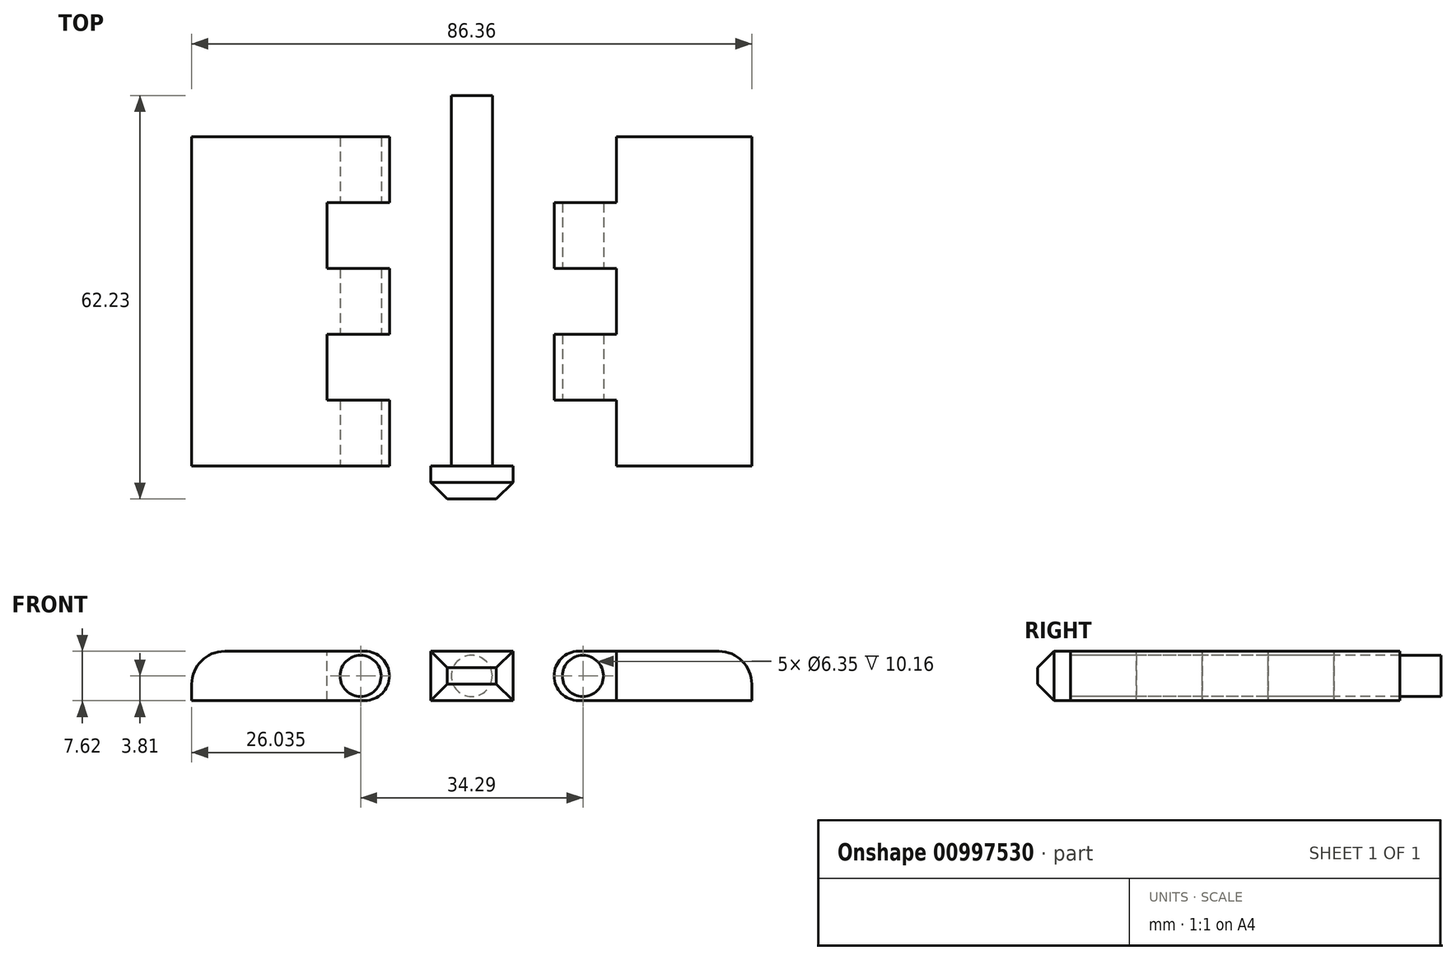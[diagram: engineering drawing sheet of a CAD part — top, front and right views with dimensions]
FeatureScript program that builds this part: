
annotation { "Feature Type Name" : "Feature", "Feature Type Description" : "" }
export const myFeature = defineFeature(function(context is Context, id is Id, definition is map)
    precondition{}
    {
        {
            var Q0;
            Q0=qCreatedBy(makeId("Top.planeOp"),FACE);
            var sketch = newSketch(context, id + "F0", { "sketchPlane" : qUnion([Q0])});
            skLineSegment(sketch, "E0.bottom", {"start": v(0, 0) * mm, "end": v(30.48, 0) * mm});
            skLineSegment(sketch, "E0.top", {"start": v(0, 50.8) * mm, "end": v(30.48, 50.8) * mm});
            skLineSegment(sketch, "E0.left", {"start": v(0, 0) * mm, "end": v(0, 50.8) * mm});
            skLineSegment(sketch, "E0.right", {"start": v(30.48, 0) * mm, "end": v(30.48, 50.8) * mm});
            skPoint(sketch, "E1.startSnap0", {"position": v(30.48, 25.4) * mm});
            skLineSegment(sketch, "E2", {"start": v(-12.7, 75.24) * mm, "end": v(-12.7, -23.42) * mm, "construction": true});
            skLineSegment(sketch, "E3.MirrorCS", {"start": v(-55.88, 0) * mm, "end": v(-55.88, 50.8) * mm});
            skLineSegment(sketch, "E4.MirrorCS", {"start": v(-25.4, 50.8) * mm, "end": v(-55.88, 50.8) * mm});
            skPoint(sketch, "E5.MirrorP", {"position": v(-55.88, 25.4) * mm});
            skLineSegment(sketch, "E6.MirrorCS", {"start": v(-25.4, 0) * mm, "end": v(-55.88, 0) * mm});
            skLineSegment(sketch, "E7.MirrorCS", {"start": v(-25.4, 0) * mm, "end": v(-25.4, 50.8) * mm});
            skSolve(sketch);
        }
        {
            var Q0;
            Q0 = qSketchRegion(id + "F0", true);
            extrude(context, id + "F1", {"entities" : qUnion([Q0]), "depth" : 7.62 * mm, "offsetDistance" : 25.4 * mm});
        }
        {
            var Q0;
            Q0=makeQuery(id+"F1.opExtrude","SWEPT_FACE",FACE,{"disambiguationData":[OSD([sQuery(id+"F0.wireOp",EDGE,"E6.MirrorCS")])]});
            var sketch = newSketch(context, id + "F2", { "sketchPlane" : qUnion([Q0])});
            skPoint(sketch, "E8.0", {"position": v(-12.7, 0) * mm});
            skLineSegment(sketch, "E9", {"start": v(-12.7, 0) * mm, "end": v(-12.7, 27.95) * mm, "construction": true});
            skCircle(sketch, "E10", {"center": v(4.45, 3.81) * mm, "radius": 3.18 * mm});
            skCircle(sketch, "E11.MirrorC", {"center": v(-29.85, 3.81) * mm, "radius": 3.18 * mm});
            skLineSegment(sketch, "E12.0", {"start": v(0, 7.62) * mm, "end": v(0, 0) * mm, "construction": true});
            skPoint(sketch, "E13", {"position": v(0, 3.81) * mm});
            skSolve(sketch);
        }
        {
            var Q0;
            Q0 = qSketchRegion(id + "F2", true);
            var Q1;
            Q1=makeQuery(id+"F1.opExtrude","SWEPT_FACE",FACE,{"disambiguationData":[OSD([sQuery(id+"F0.wireOp",EDGE,"E0.top")])]});
            extrude(context, id + "F3", {"entities" : qUnion([Q0]), "operationType" : NewBodyOperationType.REMOVE, "endBound" : BoundingType.UP_TO_SURFACE, "oppositeDirection" : true, "depth" : 25.4 * mm, "endBoundEntityFace" : qUnion([Q1]), "offsetDistance" : 25.4 * mm});
        }
        {
            var Q0;
            Q0=makeQuery(id+"F1.opExtrude","CAP_FACE",FACE,{"disambiguationData":[OSD([sQuery(id+"F0.wireOp",EDGE,"E3.MirrorCS"),sQuery(id+"F0.wireOp",EDGE,"E4.MirrorCS"),sQuery(id+"F0.wireOp",EDGE,"E6.MirrorCS"),sQuery(id+"F0.wireOp",EDGE,"E7.MirrorCS")])],"isStart":false});
            var sketch = newSketch(context, id + "F4", { "sketchPlane" : qUnion([Q0])});
            skLineSegment(sketch, "E14.0.0", {"start": v(9.63, 50.8) * mm, "end": v(0, 50.8) * mm});
            skLineSegment(sketch, "E14.0.1", {"start": v(0, 50.8) * mm, "end": v(0, 0) * mm});
            skLineSegment(sketch, "E14.0.2", {"start": v(0, 0) * mm, "end": v(30.48, 0) * mm});
            skLineSegment(sketch, "E14.0.3", {"start": v(9.63, -0.98) * mm, "end": v(9.63, 50.8) * mm});
            skLineSegment(sketch, "E15", {"start": v(0, 30.48) * mm, "end": v(9.63, 30.48) * mm});
            skLineSegment(sketch, "E16", {"start": v(0, 20.32) * mm, "end": v(9.63, 20.32) * mm});
            skLineSegment(sketch, "E17", {"start": v(9.63, 10.16) * mm, "end": v(0, 10.16) * mm});
            skLineSegment(sketch, "E18", {"start": v(0, 40.64) * mm, "end": v(9.63, 40.64) * mm});
            skLineSegment(sketch, "E19.MirrorCS", {"start": v(-55.88, 50.8) * mm, "end": v(-25.4, 50.8) * mm});
            skLineSegment(sketch, "E20.MirrorCS", {"start": v(-25.4, 40.64) * mm, "end": v(-35.03, 40.64) * mm});
            skLineSegment(sketch, "E21.MirrorCS", {"start": v(-25.4, 30.48) * mm, "end": v(-35.03, 30.48) * mm});
            skLineSegment(sketch, "E22.MirrorCS", {"start": v(-25.4, 20.32) * mm, "end": v(-35.03, 20.32) * mm});
            skLineSegment(sketch, "E23.MirrorCS", {"start": v(-35.03, 10.16) * mm, "end": v(-25.4, 10.16) * mm});
            skLineSegment(sketch, "E24.MirrorCS", {"start": v(-25.4, 0) * mm, "end": v(-55.88, 0) * mm});
            skLineSegment(sketch, "E25.MirrorCS", {"start": v(-25.4, 50.8) * mm, "end": v(-25.4, 0) * mm});
            skLineSegment(sketch, "E26.MirrorCS", {"start": v(-35.03, -0.98) * mm, "end": v(-35.03, 50.8) * mm});
            skPoint(sketch, "E27.orphan", {"position": v(30.48, 50.8) * mm});
            skSolve(sketch);
        }
        {
            var Q0;
            {var subQ3=sQuery(id+"F4.wireOp",EDGE,"E17");Q0=makeQuery(id+"F4.imprint","IMPRINT",FACE,{"disambiguationData":[TD([[makeQuery(id+"F4.imprint","IMPRINT",EDGE,{"derivedFrom":subQ3}),1.0]])]});}
            var Q1;
            {var subQ0=sQuery(id+"F4.wireOp",EDGE,"E15");Q1=makeQuery(id+"F4.imprint","IMPRINT",FACE,{"disambiguationData":[TD([[makeQuery(id+"F4.imprint","IMPRINT",EDGE,{"derivedFrom":subQ0}),-1.0]])]});}
            var Q2;
            {var subQ0=sQuery(id+"F4.wireOp",EDGE,"E14.0.0");Q2=makeQuery(id+"F4.imprint","IMPRINT",FACE,{"disambiguationData":[TD([[makeQuery(id+"F4.imprint","IMPRINT",EDGE,{"derivedFrom":subQ0}),1.0]])]});}
            var Q3;
            Q3=makeQuery(id+"F1.opExtrude","CAP_FACE",FACE,{"disambiguationData":[OSD([sQuery(id+"F0.wireOp",EDGE,"E0.bottom"),sQuery(id+"F0.wireOp",EDGE,"E0.top"),sQuery(id+"F0.wireOp",EDGE,"E0.left"),sQuery(id+"F0.wireOp",EDGE,"E0.right")])],"isStart":true});
            extrude(context, id + "F5", {"entities" : qUnion([Q0, Q1, Q2]), "operationType" : NewBodyOperationType.REMOVE, "endBound" : BoundingType.UP_TO_SURFACE, "oppositeDirection" : true, "depth" : 25.4 * mm, "endBoundEntityFace" : qUnion([Q3]), "offsetDistance" : 25.4 * mm});
        }
        {
            var Q0;
            {var subQ0=sQuery(id+"F4.wireOp",EDGE,"E22.MirrorCS");Q0=makeQuery(id+"F4.imprint","IMPRINT",FACE,{"disambiguationData":[TD([[makeQuery(id+"F4.imprint","IMPRINT",EDGE,{"derivedFrom":subQ0}),1.0]])]});}
            var Q1;
            {var subQ0=sQuery(id+"F4.wireOp",EDGE,"E20.MirrorCS");Q1=makeQuery(id+"F4.imprint","IMPRINT",FACE,{"disambiguationData":[TD([[makeQuery(id+"F4.imprint","IMPRINT",EDGE,{"derivedFrom":subQ0}),1.0]])]});}
            var Q2;
            Q2=makeQuery(id+"F1.opExtrude","CAP_FACE",FACE,{"disambiguationData":[OSD([sQuery(id+"F0.wireOp",EDGE,"E3.MirrorCS"),sQuery(id+"F0.wireOp",EDGE,"E4.MirrorCS"),sQuery(id+"F0.wireOp",EDGE,"E6.MirrorCS"),sQuery(id+"F0.wireOp",EDGE,"E7.MirrorCS")])],"isStart":true});
            extrude(context, id + "F6", {"entities" : qUnion([Q0, Q1]), "operationType" : NewBodyOperationType.REMOVE, "endBound" : BoundingType.UP_TO_SURFACE, "oppositeDirection" : true, "depth" : 25.4 * mm, "endBoundEntityFace" : qUnion([Q2]), "offsetDistance" : 25.4 * mm});
        }
        {
            var Q0;
            Q0=makeQuery(id+"F1.opExtrude","CAP_EDGE",EDGE,{"disambiguationData":[OSD([sQuery(id+"F0.wireOp",EDGE,"E3.MirrorCS")])],"isStart":false});
            var Q1;
            Q1=makeQuery(id+"F1.opExtrude","CAP_EDGE",EDGE,{"disambiguationData":[OSD([sQuery(id+"F0.wireOp",EDGE,"E0.right")])],"isStart":false});
            fillet(context, id + "F7", {"entities" : qUnion([Q0, Q1]), "radius" : 5.08 * mm, "tangentPropagation" : true, "allowEdgeOverflow" : false});
        }
        {
            var Q0;
            {var subQ0=sQuery(id+"F0.wireOp",EDGE,"E0.left");Q0=makeQuery(id+"F5.boolean.opBoolean","SPLIT",EDGE,{"disambiguationData":[TD([makeQuery(id+"F5.opExtrude","SWEPT_FACE",FACE,{"disambiguationData":[OSD([sQuery(id+"F4.wireOp",EDGE,"E16")])]})])],"derivedFrom":makeQuery(id+"F1.opExtrude","CAP_EDGE",EDGE,{"disambiguationData":[OSD([subQ0])],"isStart":false})});}
            var Q1;
            {var subQ0=sQuery(id+"F0.wireOp",EDGE,"E0.left");Q1=makeQuery(id+"F5.boolean.opBoolean","SPLIT",EDGE,{"disambiguationData":[TD([makeQuery(id+"F5.opExtrude","SWEPT_FACE",FACE,{"disambiguationData":[OSD([sQuery(id+"F4.wireOp",EDGE,"E16")])]})])],"derivedFrom":makeQuery(id+"F1.opExtrude","CAP_EDGE",EDGE,{"disambiguationData":[OSD([subQ0])],"isStart":true})});}
            var Q2;
            {var subQ0=sQuery(id+"F0.wireOp",EDGE,"E0.left");Q2=makeQuery(id+"F5.boolean.opBoolean","SPLIT",EDGE,{"disambiguationData":[TD([makeQuery(id+"F5.opExtrude","SWEPT_FACE",FACE,{"disambiguationData":[OSD([sQuery(id+"F4.wireOp",EDGE,"E15")])]})])],"derivedFrom":makeQuery(id+"F1.opExtrude","CAP_EDGE",EDGE,{"disambiguationData":[OSD([subQ0])],"isStart":false})});}
            var Q3;
            {var subQ0=sQuery(id+"F0.wireOp",EDGE,"E0.left");Q3=makeQuery(id+"F5.boolean.opBoolean","SPLIT",EDGE,{"disambiguationData":[TD([makeQuery(id+"F5.opExtrude","SWEPT_FACE",FACE,{"disambiguationData":[OSD([sQuery(id+"F4.wireOp",EDGE,"E15")])]})])],"derivedFrom":makeQuery(id+"F1.opExtrude","CAP_EDGE",EDGE,{"disambiguationData":[OSD([subQ0])],"isStart":true})});}
            var Q4;
            {var subQ0=sQuery(id+"F0.wireOp",EDGE,"E7.MirrorCS");var subQ1=sQuery(id+"F0.wireOp",EDGE,"E6.MirrorCS");Q4=makeQuery(id+"F6.boolean.opBoolean","SPLIT",EDGE,{"disambiguationData":[TD([makeQuery(id+"F1.opExtrude","SWEPT_FACE",FACE,{"disambiguationData":[OSD([subQ1])]})])],"derivedFrom":makeQuery(id+"F1.opExtrude","CAP_EDGE",EDGE,{"disambiguationData":[OSD([subQ0])],"isStart":true})});}
            var Q5;
            {var subQ0=sQuery(id+"F0.wireOp",EDGE,"E7.MirrorCS");var subQ1=sQuery(id+"F0.wireOp",EDGE,"E6.MirrorCS");Q5=makeQuery(id+"F6.boolean.opBoolean","SPLIT",EDGE,{"disambiguationData":[TD([makeQuery(id+"F1.opExtrude","SWEPT_FACE",FACE,{"disambiguationData":[OSD([subQ1])]})])],"derivedFrom":makeQuery(id+"F1.opExtrude","CAP_EDGE",EDGE,{"disambiguationData":[OSD([subQ0])],"isStart":false})});}
            var Q6;
            {var subQ0=sQuery(id+"F0.wireOp",EDGE,"E7.MirrorCS");Q6=makeQuery(id+"F6.boolean.opBoolean","SPLIT",EDGE,{"disambiguationData":[TD([makeQuery(id+"F6.opExtrude","SWEPT_FACE",FACE,{"disambiguationData":[OSD([sQuery(id+"F4.wireOp",EDGE,"E21.MirrorCS")])]})])],"derivedFrom":makeQuery(id+"F1.opExtrude","CAP_EDGE",EDGE,{"disambiguationData":[OSD([subQ0])],"isStart":true})});}
            var Q7;
            {var subQ0=sQuery(id+"F0.wireOp",EDGE,"E7.MirrorCS");Q7=makeQuery(id+"F6.boolean.opBoolean","SPLIT",EDGE,{"disambiguationData":[TD([makeQuery(id+"F6.opExtrude","SWEPT_FACE",FACE,{"disambiguationData":[OSD([sQuery(id+"F4.wireOp",EDGE,"E21.MirrorCS")])]})])],"derivedFrom":makeQuery(id+"F1.opExtrude","CAP_EDGE",EDGE,{"disambiguationData":[OSD([subQ0])],"isStart":false})});}
            var Q8;
            {var subQ0=sQuery(id+"F0.wireOp",EDGE,"E7.MirrorCS");var subQ1=sQuery(id+"F0.wireOp",EDGE,"E4.MirrorCS");Q8=makeQuery(id+"F6.boolean.opBoolean","SPLIT",EDGE,{"disambiguationData":[TD([makeQuery(id+"F1.opExtrude","SWEPT_FACE",FACE,{"disambiguationData":[OSD([subQ1])]})])],"derivedFrom":makeQuery(id+"F1.opExtrude","CAP_EDGE",EDGE,{"disambiguationData":[OSD([subQ0])],"isStart":true})});}
            var Q9;
            {var subQ0=sQuery(id+"F0.wireOp",EDGE,"E7.MirrorCS");var subQ1=sQuery(id+"F0.wireOp",EDGE,"E4.MirrorCS");Q9=makeQuery(id+"F6.boolean.opBoolean","SPLIT",EDGE,{"disambiguationData":[TD([makeQuery(id+"F1.opExtrude","SWEPT_FACE",FACE,{"disambiguationData":[OSD([subQ1])]})])],"derivedFrom":makeQuery(id+"F1.opExtrude","CAP_EDGE",EDGE,{"disambiguationData":[OSD([subQ0])],"isStart":false})});}
            fillet(context, id + "F8", {"entities" : qUnion([Q0, Q1, Q2, Q3, Q4, Q5, Q6, Q7, Q8, Q9]), "radius" : 3.8 * mm, "tangentPropagation" : true, "allowEdgeOverflow" : false});
        }
        {
            var Q0;
            Q0=makeQuery(id+"F1.opExtrude","SWEPT_FACE",FACE,{"disambiguationData":[OSD([sQuery(id+"F0.wireOp",EDGE,"E6.MirrorCS")])]});
            var sketch = newSketch(context, id + "F9", { "sketchPlane" : qUnion([Q0])});
            skCircle(sketch, "E28", {"center": v(-12.7, 3.81) * mm, "radius": 3.18 * mm});
            skPoint(sketch, "E28.centerSnap0", {"position": v(-25.4, 3.81) * mm});
            skLineSegment(sketch, "E29", {"start": v(-12.7, -14.58) * mm, "end": v(-12.7, 0) * mm, "construction": true});
            skPoint(sketch, "E30.0", {"position": v(-12.7, 0) * mm});
            skLineSegment(sketch, "E31.bottom", {"start": v(-6.35, 7.62) * mm, "end": v(-19.05, 7.62) * mm});
            skLineSegment(sketch, "E31.top", {"start": v(-6.35, 0) * mm, "end": v(-19.05, 0) * mm});
            skLineSegment(sketch, "E31.left", {"start": v(-6.35, 7.62) * mm, "end": v(-6.35, 0) * mm});
            skLineSegment(sketch, "E31.right", {"start": v(-19.05, 7.62) * mm, "end": v(-19.05, 0) * mm});
            skSolve(sketch);
        }
        {
            var Q0;
            Q0 = qSketchRegion(id + "F9", true);
            var Q1;
            Q1=makeQuery(id+"F9.imprint","IMPRINT",FACE,{"disambiguationData":[TD([[makeQuery(id+"F9.imprint","IMPRINT",EDGE,{"derivedFrom":sQuery(id+"F9.wireOp",EDGE,"E28")}),1.0]])]});
            extrude(context, id + "F10", {"entities" : qUnion([Q0, Q1]), "depth" : 5.08 * mm, "offsetDistance" : 25.4 * mm});
        }
        {
            var Q0;
            Q0=makeQuery(id+"F9.imprint","IMPRINT",FACE,{"disambiguationData":[TD([[makeQuery(id+"F9.imprint","IMPRINT",EDGE,{"derivedFrom":sQuery(id+"F9.wireOp",EDGE,"E28")}),1.0]])]});
            extrude(context, id + "F11", {"entities" : qUnion([Q0]), "operationType" : NewBodyOperationType.ADD, "oppositeDirection" : true, "depth" : 57.15 * mm, "offsetDistance" : 25.4 * mm});
        }
        {
            var Q0;
            Q0=makeQuery(id+"F10.opExtrude","CAP_FACE",FACE,{"disambiguationData":[OSD([sQuery(id+"F9.wireOp",EDGE,"E31.bottom"),sQuery(id+"F9.wireOp",EDGE,"E31.top"),sQuery(id+"F9.wireOp",EDGE,"E31.left"),sQuery(id+"F9.wireOp",EDGE,"E31.right")])],"isStart":false});
            chamfer(context, id + "F12", {"entities" : qUnion([Q0]), "width" : 2.54 * mm, "tangentPropagation" : true});
        }
    });
